# Revit family: Haworth_Atwell_Chair
name_source: partatom
category: Furniture
revit_build: Autodesk Revit 2018 (Build: 20170223_1515(x64)
units: mm (PartAtom-declared; Revit-internal decimal feet)

## family parameters
Always vertical = Yes
Cut with Voids When Loaded = No
OmniClass Number = 23.40.20.00
OmniClass Title = General Furniture and Specialties
Room Calculation Point = No
Shared = No
Work Plane-Based = No

## types (2) — shared parameters
Actual Depth = 2' - 6"
Actual Height = 3' - 0 1/2"
Actual Width = 2' - 1 1/2"
Assembly Code = E2020200
Manufacturer = Haworth
Model = Haworth Atwell
Size = Verify Final Dim. w/ Haworth
URL = http://healthcare.haworth.com
URL - Product = http://healthcare.haworth.com
Version = 0
Warranty = http://healthcare.haworth.com

## per-type parameters (varying)
| type | Description | With Arms | Without Arms |
| HE901-SC - Without Arms | Haworth Atwell Chair - Without Arms | No | Yes |
| HE901-AC - With Arms | Haworth Atwell Chair - With Arms | Yes | No |

## geometry (parser evidence)
native form markers: Sweep x8
no freeform markers — native parametric forms only
